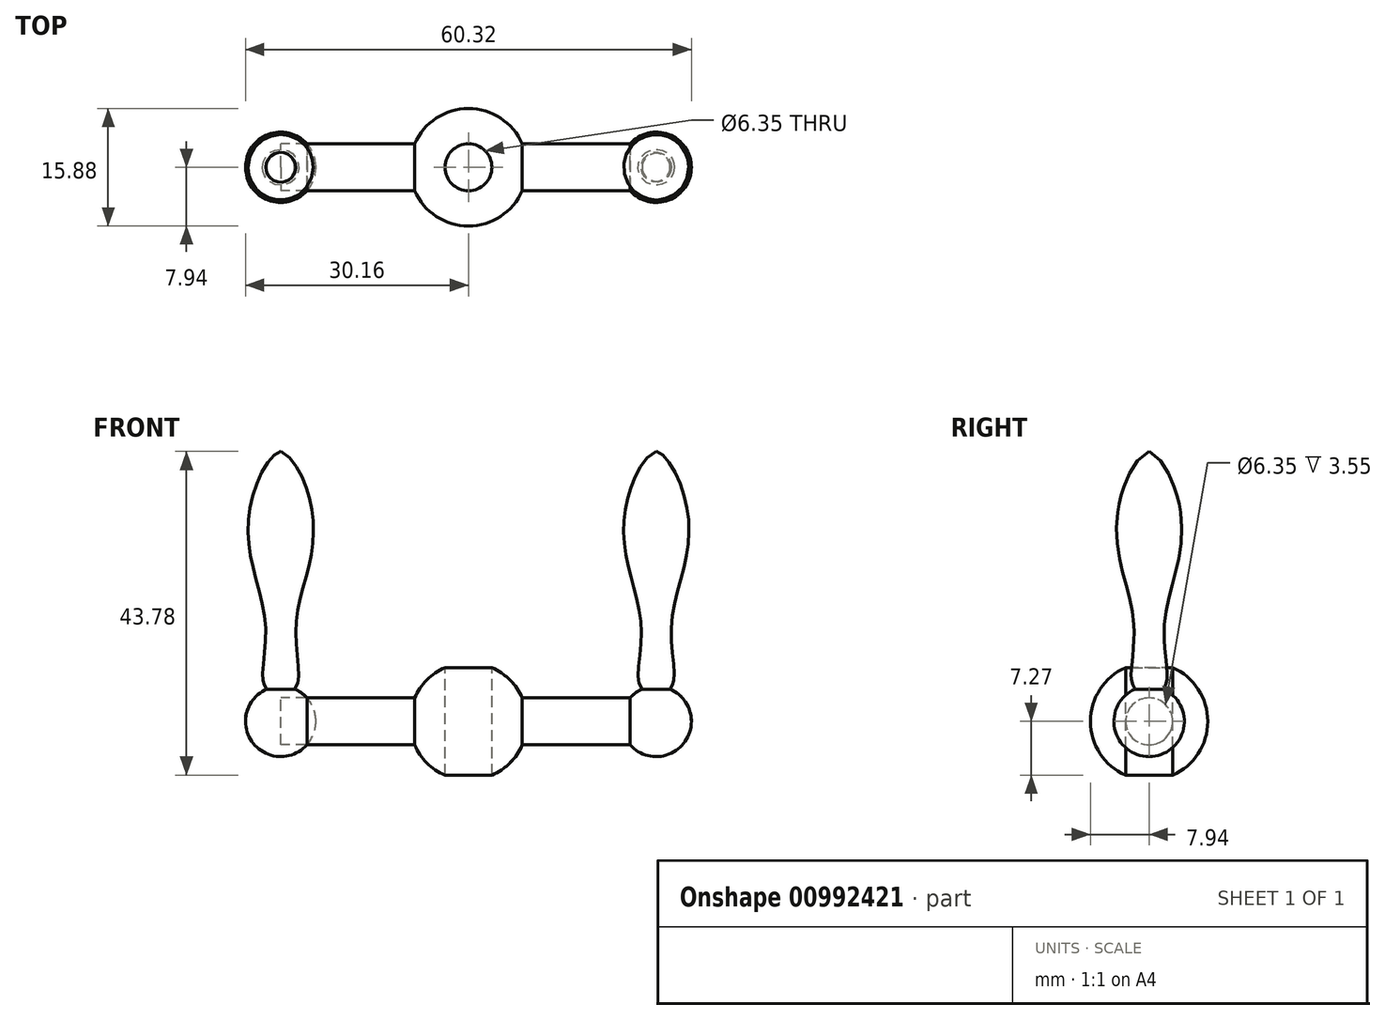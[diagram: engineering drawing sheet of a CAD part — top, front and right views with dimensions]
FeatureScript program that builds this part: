
annotation { "Feature Type Name" : "Feature", "Feature Type Description" : "" }
export const myFeature = defineFeature(function(context is Context, id is Id, definition is map)
    precondition{}
    {
        {
            var Q0;
            Q0=qCreatedBy(makeId("Front.planeOp"),FACE);
            var sketch = newSketch(context, id + "F0", { "sketchPlane" : qUnion([Q0])});
            skCircle(sketch, "E0", {"center": v(0, 0) * mm, "radius": 7.94 * mm});
            skLineSegment(sketch, "E1.bottom", {"start": v(25.4, 3.18) * mm, "end": v(-25.4, 3.18) * mm});
            skLineSegment(sketch, "E1.top", {"start": v(25.4, -3.17) * mm, "end": v(-25.4, -3.17) * mm});
            skLineSegment(sketch, "E1.left", {"start": v(25.4, 3.18) * mm, "end": v(25.4, -3.18) * mm});
            skLineSegment(sketch, "E1.right", {"start": v(-25.4, 3.18) * mm, "end": v(-25.4, -3.18) * mm});
            skCircle(sketch, "E2", {"center": v(-25.4, 0) * mm, "radius": 4.76 * mm});
            skCircle(sketch, "E3", {"center": v(25.4, 0) * mm, "radius": 4.76 * mm});
            skLineSegment(sketch, "E4", {"start": v(-25.4, 4.76) * mm, "end": v(-25.4, 36.51) * mm});
            skFitSpline(sketch, "E5", {"points": [v(-25.4, 36.51) * mm, v(-29.09, 30.86) * mm, v(-29.43, 22.1) * mm, v(-27.45, 12.85) * mm, v(-27.82, 5.78) * mm, v(-27.3, 4.37) * mm], "startDerivative": vector(-20.49, -4.9) * mm, "endDerivative": vector(7.26, -13) * mm});
            skFitSpline(sketch, "E6.MirrorCS", {"points": [v(25.4, 36.51) * mm, v(29.09, 30.86) * mm, v(29.43, 22.1) * mm, v(27.45, 12.85) * mm, v(27.82, 5.78) * mm, v(27.3, 4.37) * mm], "startDerivative": vector(20.49, -4.9) * mm, "endDerivative": vector(-7.26, -13) * mm});
            skLineSegment(sketch, "E7.MirrorCS", {"start": v(25.4, 4.76) * mm, "end": v(25.4, 36.51) * mm});
            skLineSegment(sketch, "E8", {"start": v(0, 49.5) * mm, "end": v(0, -59.8) * mm});
            skLineSegment(sketch, "E9", {"start": v(-25.4, 48.7) * mm, "end": v(-25.4, -19.26) * mm});
            skLineSegment(sketch, "E10", {"start": v(25.4, 46.2) * mm, "end": v(25.4, -18.33) * mm});
            skLineSegment(sketch, "E11", {"start": v(-39.17, 0) * mm, "end": v(39.78, 0) * mm});
            skLineSegment(sketch, "E12.bottom", {"start": v(3.17, 12.7) * mm, "end": v(-3.18, 12.7) * mm});
            skLineSegment(sketch, "E12.top", {"start": v(3.18, -12.7) * mm, "end": v(-3.17, -12.7) * mm});
            skLineSegment(sketch, "E12.left", {"start": v(3.17, 12.7) * mm, "end": v(3.18, -12.7) * mm});
            skLineSegment(sketch, "E12.right", {"start": v(-3.18, 12.7) * mm, "end": v(-3.17, -12.7) * mm});
            skSolve(sketch);
        }
        {
            var Q0;
            {var subQ0=sQuery(id+"F0.wireOp",EDGE,"E1.bottom");var subQ1=sQuery(id+"F0.wireOp",EDGE,"E0");var subQ2=makeQuery(id+"F0.imprint","INTERSECT",VERTEX,{"disambiguationData":[OD(1.0)],"derivedFrom":[subQ1,subQ0]});Q0=makeQuery(id+"F0.imprint","IMPRINT",FACE,{"disambiguationData":[TD([[makeQuery(id+"F0.imprint","IMPRINT",EDGE,{"disambiguationData":[TD([[subQ2,-1.0]])],"derivedFrom":subQ1}),1.0]])]});}
            var Q1;
            {var subQ0=sQuery(id+"F0.wireOp",EDGE,"E1.top");var subQ1=sQuery(id+"F0.wireOp",EDGE,"E0");var subQ2=makeQuery(id+"F0.imprint","INTERSECT",VERTEX,{"disambiguationData":[OD(0.0)],"derivedFrom":[subQ1,subQ0]});Q1=makeQuery(id+"F0.imprint","IMPRINT",FACE,{"disambiguationData":[TD([[makeQuery(id+"F0.imprint","IMPRINT",EDGE,{"disambiguationData":[TD([[subQ2,1.0]])],"derivedFrom":subQ1}),1.0]])]});}
            var Q2;
            {var subQ0=sQuery(id+"F0.wireOp",EDGE,"E12.right");var subQ1=sQuery(id+"F0.wireOp",EDGE,"E0");var subQ2=makeQuery(id+"F0.imprint","INTERSECT",VERTEX,{"disambiguationData":[OD(0.0)],"derivedFrom":[subQ1,subQ0]});Q2=makeQuery(id+"F0.imprint","IMPRINT",FACE,{"disambiguationData":[TD([[makeQuery(id+"F0.imprint","IMPRINT",EDGE,{"disambiguationData":[TD([[subQ2,-1.0]])],"derivedFrom":subQ1}),1.0]])]});}
            var Q3;
            {var subQ0=sQuery(id+"F0.wireOp",EDGE,"E1.top");var subQ1=sQuery(id+"F0.wireOp",EDGE,"E0");var subQ2=makeQuery(id+"F0.imprint","INTERSECT",VERTEX,{"disambiguationData":[OD(0.0)],"derivedFrom":[subQ1,subQ0]});Q3=makeQuery(id+"F0.imprint","IMPRINT",FACE,{"disambiguationData":[TD([[makeQuery(id+"F0.imprint","IMPRINT",EDGE,{"disambiguationData":[TD([[subQ2,-1.0]])],"derivedFrom":subQ1}),1.0]])]});}
            var Q4;
            Q4=sQuery(id+"F0.wireOp",EDGE,"E8");
            revolve(context, id + "F1", {"surfaceOperationType" : NewSurfaceOperationType.NEW, "entities" : qUnion([Q0, Q1, Q2, Q3]), "axis" : qUnion([Q4]), "revolveType" : RevolveType.FULL});
        }
        {
            var Q0;
            {var subQ0=sQuery(id+"F0.wireOp",EDGE,"E1.bottom");var subQ1=sQuery(id+"F0.wireOp",EDGE,"E0");var subQ2=makeQuery(id+"F0.imprint","INTERSECT",VERTEX,{"disambiguationData":[OD(1.0)],"derivedFrom":[subQ1,subQ0]});Q0=makeQuery(id+"F0.imprint","IMPRINT",FACE,{"disambiguationData":[TD([[makeQuery(id+"F0.imprint","IMPRINT",EDGE,{"disambiguationData":[TD([[subQ2,-1.0]])],"derivedFrom":subQ1}),-1.0]])]});}
            var Q1;
            {var subQ0=sQuery(id+"F0.wireOp",EDGE,"E1.bottom");var subQ1=sQuery(id+"F0.wireOp",EDGE,"E0");var subQ2=makeQuery(id+"F0.imprint","INTERSECT",VERTEX,{"disambiguationData":[OD(0.0)],"derivedFrom":[subQ1,subQ0]});Q1=makeQuery(id+"F0.imprint","IMPRINT",FACE,{"disambiguationData":[TD([[makeQuery(id+"F0.imprint","IMPRINT",EDGE,{"disambiguationData":[TD([[subQ2,1.0]])],"derivedFrom":subQ1}),-1.0]])]});}
            var Q2;
            {var subQ0=sQuery(id+"F0.wireOp",EDGE,"E2");var subQ1=makeQuery(id+"F0.imprint","INTERSECT",VERTEX,{"derivedFrom":[subQ0,sQuery(id+"F0.wireOp",EDGE,"E5")]});Q2=makeQuery(id+"F0.imprint","IMPRINT",FACE,{"disambiguationData":[TD([[makeQuery(id+"F0.imprint","IMPRINT",EDGE,{"disambiguationData":[TD([[subQ1,-1.0]])],"derivedFrom":subQ0}),1.0]])]});}
            var Q3;
            {var subQ3=sQuery(id+"F0.wireOp",EDGE,"E2");var subQ5=sQuery(id+"F0.wireOp",EDGE,"E11");var subQ7=makeQuery(id+"F0.imprint","INTERSECT",VERTEX,{"disambiguationData":[OD(0.0)],"derivedFrom":[subQ3,subQ5]});Q3=makeQuery(id+"F0.imprint","IMPRINT",FACE,{"disambiguationData":[TD([[makeQuery(id+"F0.imprint","IMPRINT",EDGE,{"disambiguationData":[TD([[subQ7,-1.0]])],"derivedFrom":subQ3}),1.0]])]});}
            var Q4;
            {var subQ1=sQuery(id+"F0.wireOp",EDGE,"E1.bottom");var subQ3=sQuery(id+"F0.wireOp",EDGE,"E2");var subQ4=makeQuery(id+"F0.imprint","INTERSECT",VERTEX,{"derivedFrom":[subQ1,subQ3]});Q4=makeQuery(id+"F0.imprint","IMPRINT",FACE,{"disambiguationData":[TD([[makeQuery(id+"F0.imprint","IMPRINT",EDGE,{"disambiguationData":[TD([[subQ4,-1.0]])],"derivedFrom":subQ1}),-1.0]])]});}
            var Q5;
            {var subQ0=sQuery(id+"F0.wireOp",EDGE,"E3");var subQ1=sQuery(id+"F0.wireOp",EDGE,"E1.bottom");var subQ2=makeQuery(id+"F0.imprint","INTERSECT",VERTEX,{"derivedFrom":[subQ1,subQ0]});Q5=makeQuery(id+"F0.imprint","IMPRINT",FACE,{"disambiguationData":[TD([[makeQuery(id+"F0.imprint","IMPRINT",EDGE,{"disambiguationData":[TD([[subQ2,-1.0]])],"derivedFrom":subQ0}),1.0]])]});}
            var Q6;
            {var subQ0=sQuery(id+"F0.wireOp",EDGE,"E3");var subQ1=sQuery(id+"F0.wireOp",EDGE,"E1.bottom");var subQ2=makeQuery(id+"F0.imprint","INTERSECT",VERTEX,{"derivedFrom":[subQ1,subQ0]});Q6=makeQuery(id+"F0.imprint","IMPRINT",FACE,{"disambiguationData":[TD([[makeQuery(id+"F0.imprint","IMPRINT",EDGE,{"disambiguationData":[TD([[subQ2,1.0]])],"derivedFrom":subQ1}),-1.0]])]});}
            var Q7;
            {var subQ3=sQuery(id+"F0.wireOp",EDGE,"E3");var subQ5=makeQuery(id+"F0.imprint","INTERSECT",VERTEX,{"derivedFrom":[subQ3,sQuery(id+"F0.wireOp",EDGE,"E6.MirrorCS")]});Q7=makeQuery(id+"F0.imprint","IMPRINT",FACE,{"disambiguationData":[TD([[makeQuery(id+"F0.imprint","IMPRINT",EDGE,{"disambiguationData":[TD([[subQ5,1.0]])],"derivedFrom":subQ3}),1.0]])]});}
            var Q8;
            Q8=sQuery(id+"F0.wireOp",EDGE,"E11");
            revolve(context, id + "F2", {"operationType" : NewBodyOperationType.ADD, "surfaceOperationType" : NewSurfaceOperationType.NEW, "entities" : qUnion([Q0, Q1, Q2, Q3, Q4, Q5, Q6, Q7]), "axis" : qUnion([Q8]), "revolveType" : RevolveType.FULL});
        }
        {
            var Q0;
            {var subQ0=sQuery(id+"F0.wireOp",EDGE,"E4");Q0=makeQuery(id+"F0.imprint","IMPRINT",FACE,{"disambiguationData":[TD([[makeQuery(id+"F0.imprint","IMPRINT",EDGE,{"derivedFrom":subQ0}),1.0]])]});}
            var Q1;
            Q1=sQuery(id+"F0.wireOp",EDGE,"E9");
            revolve(context, id + "F3", {"operationType" : NewBodyOperationType.ADD, "surfaceOperationType" : NewSurfaceOperationType.NEW, "entities" : qUnion([Q0]), "axis" : qUnion([Q1]), "revolveType" : RevolveType.FULL});
        }
        {
            var Q0;
            {var subQ0=sQuery(id+"F0.wireOp",EDGE,"E6.MirrorCS");Q0=makeQuery(id+"F0.imprint","IMPRINT",FACE,{"disambiguationData":[TD([[makeQuery(id+"F0.imprint","IMPRINT",EDGE,{"derivedFrom":subQ0}),-1.0]])]});}
            var Q1;
            Q1=sQuery(id+"F0.wireOp",EDGE,"E10");
            revolve(context, id + "F4", {"operationType" : NewBodyOperationType.ADD, "surfaceOperationType" : NewSurfaceOperationType.NEW, "entities" : qUnion([Q0]), "axis" : qUnion([Q1]), "revolveType" : RevolveType.FULL});
        }
    });
